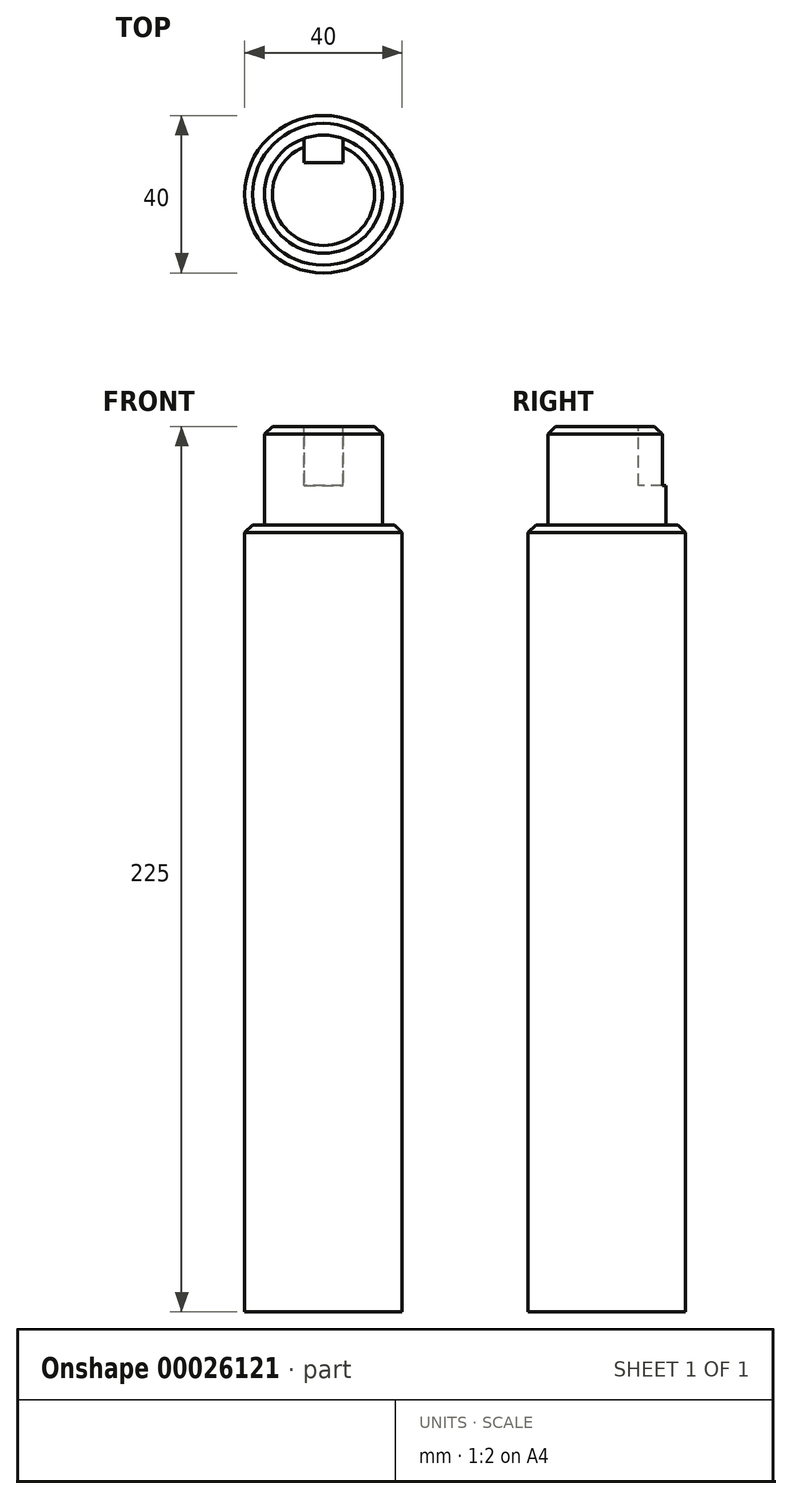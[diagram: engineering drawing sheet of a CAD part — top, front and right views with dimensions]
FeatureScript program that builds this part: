
annotation { "Feature Type Name" : "Feature", "Feature Type Description" : "" }
export const myFeature = defineFeature(function(context is Context, id is Id, definition is map)
    precondition{}
    {
        {
            var Q0;
            Q0=qCreatedBy(makeId("Top.planeOp"),FACE);
            var sketch = newSketch(context, id + "F0", { "sketchPlane" : qUnion([Q0])});
            skPoint(sketch, "E0.0.midPoint", {"position": v(-24.03, 29.06) * mm});
            skCircle(sketch, "E1", {"center": v(0, 0) * mm, "radius": 20 * mm});
            skSolve(sketch);
        }
        {
            var Q0;
            Q0 = qSketchRegion(id + "F0", true);
            extrude(context, id + "F1", {"entities" : qUnion([Q0]), "depth" : 200 * mm});
        }
        {
            var Q0;
            Q0=makeQuery(id+"F1.opExtrude","CAP_FACE",FACE,{"disambiguationData":[OSD([sQuery(id+"F0.wireOp",EDGE,"E1")])],"isStart":false});
            var sketch = newSketch(context, id + "F2", { "sketchPlane" : qUnion([Q0])});
            skCircle(sketch, "E2", {"center": v(0, 0) * mm, "radius": 15 * mm});
            skSolve(sketch);
        }
        {
            var Q0;
            Q0=makeQuery(id+"F2.imprint","IMPRINT",FACE,{"disambiguationData":[TD([[makeQuery(id+"F2.imprint","IMPRINT",EDGE,{"derivedFrom":sQuery(id+"F2.wireOp",EDGE,"E2")}),1.0]])]});
            extrude(context, id + "F3", {"entities" : qUnion([Q0]), "operationType" : NewBodyOperationType.ADD, "depth" : 25 * mm});
        }
        {
            var Q0;
            Q0=makeQuery(id+"F3.opExtrude","CAP_EDGE",EDGE,{"disambiguationData":[OSD([sQuery(id+"F2.wireOp",EDGE,"E2")])],"isStart":false});
            var Q1;
            Q1=makeQuery(id+"F1.opExtrude","CAP_EDGE",EDGE,{"disambiguationData":[OSD([sQuery(id+"F0.wireOp",EDGE,"E1")])],"isStart":false});
            chamfer(context, id + "F4", {"entities" : qUnion([Q0, Q1]), "width" : 2 * mm, "tangentPropagation" : true});
        }
        {
            var Q0;
            Q0=makeQuery(id+"F3.opExtrude","CAP_FACE",FACE,{"disambiguationData":[OSD([sQuery(id+"F2.wireOp",EDGE,"E2")])],"isStart":false});
            var sketch = newSketch(context, id + "F5", { "sketchPlane" : qUnion([Q0])});
            skLineSegment(sketch, "E3.bottom", {"start": v(-5, 24.07) * mm, "end": v(5, 24.07) * mm});
            skLineSegment(sketch, "E3.top", {"start": v(-5, 8) * mm, "end": v(5, 8) * mm});
            skLineSegment(sketch, "E3.left", {"start": v(-5, 24.07) * mm, "end": v(-5, 8) * mm});
            skLineSegment(sketch, "E3.right", {"start": v(5, 24.07) * mm, "end": v(5, 8) * mm});
            skLineSegment(sketch, "E4", {"start": v(0, 8) * mm, "end": v(0, 0) * mm, "construction": true});
            skSolve(sketch);
        }
        {
            var Q0;
            {var subQ6=sQuery(id+"F5.wireOp",EDGE,"E3.top");Q0=makeQuery(id+"F5.imprint","IMPRINT",FACE,{"disambiguationData":[TD([[makeQuery(id+"F5.imprint","IMPRINT",EDGE,{"derivedFrom":subQ6}),1.0]])]});}
            var Q1;
            {var subQ6=sQuery(id+"F5.wireOp",EDGE,"E3.bottom");Q1=makeQuery(id+"F5.imprint","IMPRINT",FACE,{"disambiguationData":[TD([[makeQuery(id+"F5.imprint","IMPRINT",EDGE,{"derivedFrom":subQ6}),-1.0]])]});}
            extrude(context, id + "F6", {"entities" : qUnion([Q0, Q1]), "operationType" : NewBodyOperationType.REMOVE, "oppositeDirection" : true, "depth" : 15 * mm});
        }
    });
